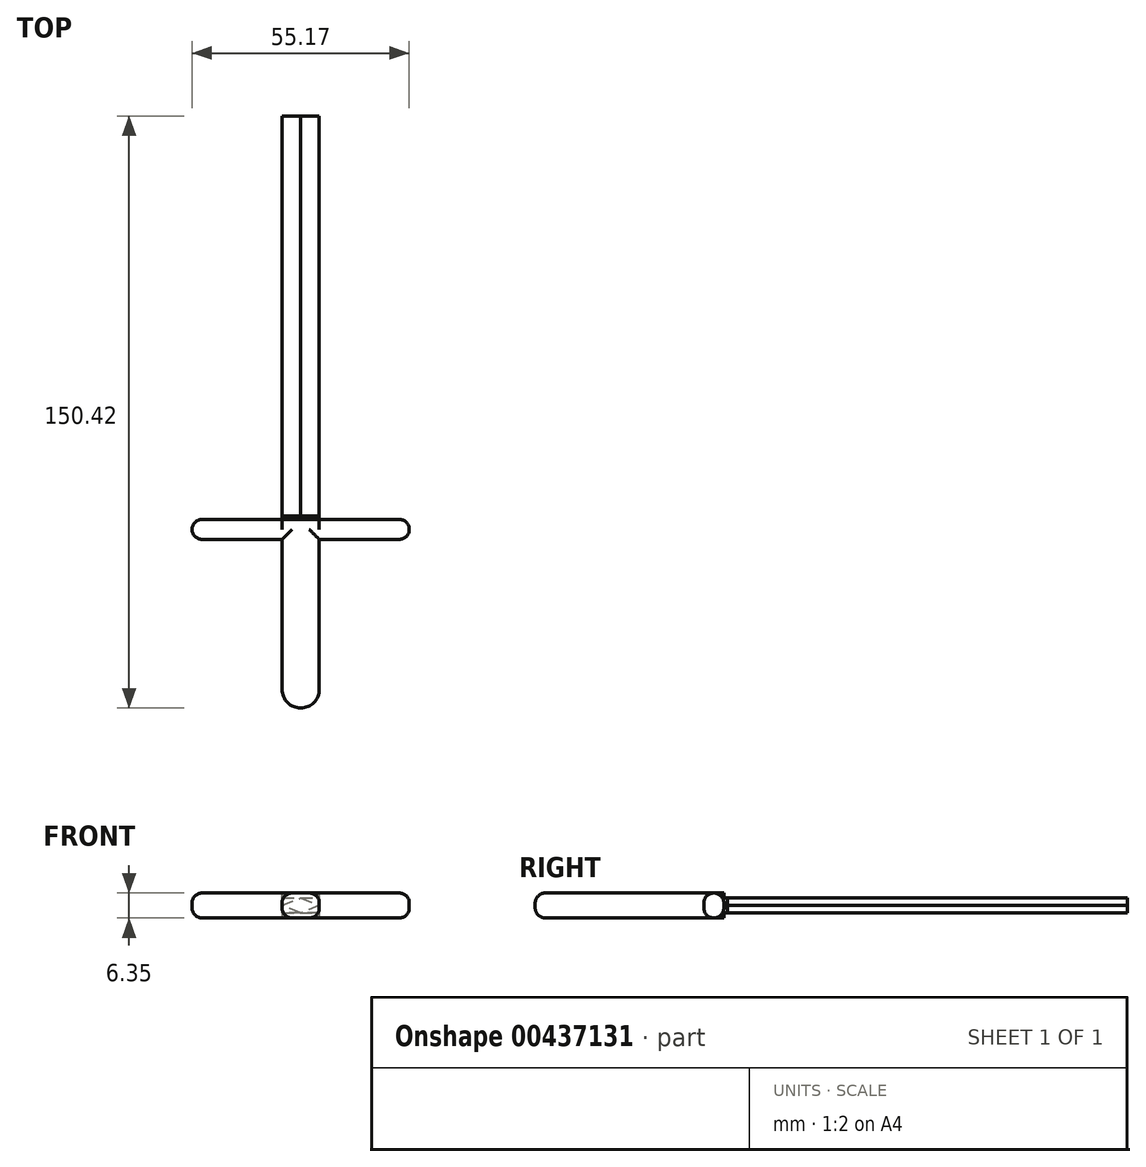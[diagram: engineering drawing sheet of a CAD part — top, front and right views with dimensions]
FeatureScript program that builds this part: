
annotation { "Feature Type Name" : "Feature", "Feature Type Description" : "" }
export const myFeature = defineFeature(function(context is Context, id is Id, definition is map)
    precondition{}
    {
        {
            var Q0;
            Q0=qCreatedBy(makeId("Top.planeOp"),FACE);
            var sketch = newSketch(context, id + "F0", { "sketchPlane" : qUnion([Q0])});
            skLineSegment(sketch, "E0.bottom", {"start": v(0, 0) * mm, "end": v(9.45, 0) * mm});
            skLineSegment(sketch, "E0.top", {"start": v(0, 62.33) * mm, "end": v(9.45, 62.33) * mm});
            skLineSegment(sketch, "E0.left", {"start": v(0, 0) * mm, "end": v(0, 62.33) * mm});
            skLineSegment(sketch, "E0.right", {"start": v(9.45, 0) * mm, "end": v(9.45, 62.33) * mm});
            skLineSegment(sketch, "E1", {"start": v(4.72, 0) * mm, "end": v(4.72, 75.05) * mm});
            skPoint(sketch, "E1.endSnap0", {"position": v(4.72, 62.33) * mm});
            skLineSegment(sketch, "E2", {"start": v(4.72, 75.05) * mm, "end": v(0, 62.33) * mm});
            skLineSegment(sketch, "E3", {"start": v(9.45, 62.33) * mm, "end": v(4.72, 75.05) * mm});
            skLineSegment(sketch, "E4", {"start": v(9.45, 0) * mm, "end": v(29.77, 0) * mm});
            skLineSegment(sketch, "E5", {"start": v(29.77, 0) * mm, "end": v(29.77, -5.08) * mm});
            skLineSegment(sketch, "E6", {"start": v(29.77, -5.08) * mm, "end": v(0, -5.08) * mm});
            skLineSegment(sketch, "E7", {"start": v(0, -5.08) * mm, "end": v(-20.32, -5.08) * mm});
            skLineSegment(sketch, "E8", {"start": v(-20.32, -5.08) * mm, "end": v(-20.32, 0) * mm});
            skLineSegment(sketch, "E9", {"start": v(-20.32, 0) * mm, "end": v(0, 0) * mm});
            skCircle(sketch, "E10", {"center": v(-20.32, -2.54) * mm, "radius": 2.54 * mm});
            skCircle(sketch, "E11", {"center": v(29.77, -2.54) * mm, "radius": 2.54 * mm});
            skLineSegment(sketch, "E12", {"start": v(0, -5.08) * mm, "end": v(0, -43.18) * mm});
            skLineSegment(sketch, "E13", {"start": v(0, -43.18) * mm, "end": v(9.45, -43.18) * mm});
            skLineSegment(sketch, "E14", {"start": v(9.45, -43.18) * mm, "end": v(9.45, -5.08) * mm});
            skCircle(sketch, "E15", {"center": v(4.72, -43.18) * mm, "radius": 4.72 * mm});
            skSolve(sketch);
        }
        {
            var Q0;
            {var subQ0=sQuery(id+"F0.wireOp",EDGE,"E0.left");Q0=makeQuery(id+"F0.imprint","IMPRINT",FACE,{"disambiguationData":[TD([[makeQuery(id+"F0.imprint","IMPRINT",EDGE,{"derivedFrom":subQ0}),-1.0]])]});}
            var Q1;
            {var subQ0=sQuery(id+"F0.wireOp",EDGE,"E0.right");Q1=makeQuery(id+"F0.imprint","IMPRINT",FACE,{"disambiguationData":[TD([[makeQuery(id+"F0.imprint","IMPRINT",EDGE,{"derivedFrom":subQ0}),1.0]])]});}
            var Q2;
            {var subQ0=sQuery(id+"F0.wireOp",EDGE,"E3");Q2=makeQuery(id+"F0.imprint","IMPRINT",FACE,{"disambiguationData":[TD([[makeQuery(id+"F0.imprint","IMPRINT",EDGE,{"derivedFrom":subQ0}),1.0]])]});}
            var Q3;
            {var subQ0=sQuery(id+"F0.wireOp",EDGE,"E2");Q3=makeQuery(id+"F0.imprint","IMPRINT",FACE,{"disambiguationData":[TD([[makeQuery(id+"F0.imprint","IMPRINT",EDGE,{"derivedFrom":subQ0}),1.0]])]});}
            var Q4;
            {var subQ5=sQuery(id+"F0.wireOp",EDGE,"E4");Q4=makeQuery(id+"F0.imprint","IMPRINT",FACE,{"disambiguationData":[TD([[makeQuery(id+"F0.imprint","IMPRINT",EDGE,{"derivedFrom":subQ5}),-1.0]])]});}
            var Q5;
            {var subQ0=sQuery(id+"F0.wireOp",EDGE,"E12");Q5=makeQuery(id+"F0.imprint","IMPRINT",FACE,{"disambiguationData":[TD([[makeQuery(id+"F0.imprint","IMPRINT",EDGE,{"derivedFrom":subQ0}),1.0]])]});}
            var Q6;
            {var subQ0=sQuery(id+"F0.wireOp",EDGE,"E8");Q6=makeQuery(id+"F0.imprint","IMPRINT",FACE,{"disambiguationData":[TD([[makeQuery(id+"F0.imprint","IMPRINT",EDGE,{"derivedFrom":subQ0}),-1.0]])]});}
            var Q7;
            {var subQ0=sQuery(id+"F0.wireOp",EDGE,"E8");Q7=makeQuery(id+"F0.imprint","IMPRINT",FACE,{"disambiguationData":[TD([[makeQuery(id+"F0.imprint","IMPRINT",EDGE,{"derivedFrom":subQ0}),1.0]])]});}
            var Q8;
            {var subQ0=sQuery(id+"F0.wireOp",EDGE,"E5");Q8=makeQuery(id+"F0.imprint","IMPRINT",FACE,{"disambiguationData":[TD([[makeQuery(id+"F0.imprint","IMPRINT",EDGE,{"derivedFrom":subQ0}),-1.0]])]});}
            var Q9;
            {var subQ0=sQuery(id+"F0.wireOp",EDGE,"E5");Q9=makeQuery(id+"F0.imprint","IMPRINT",FACE,{"disambiguationData":[TD([[makeQuery(id+"F0.imprint","IMPRINT",EDGE,{"derivedFrom":subQ0}),1.0]])]});}
            var Q10;
            {var subQ0=sQuery(id+"F0.wireOp",EDGE,"E13");Q10=makeQuery(id+"F0.imprint","IMPRINT",FACE,{"disambiguationData":[TD([[makeQuery(id+"F0.imprint","IMPRINT",EDGE,{"derivedFrom":subQ0}),-1.0]])]});}
            var Q11;
            {var subQ0=sQuery(id+"F0.wireOp",EDGE,"E13");Q11=makeQuery(id+"F0.imprint","IMPRINT",FACE,{"disambiguationData":[TD([[makeQuery(id+"F0.imprint","IMPRINT",EDGE,{"derivedFrom":subQ0}),1.0]])]});}
            extrude(context, id + "F1", {"entities" : qUnion([Q0, Q1, Q2, Q3, Q4, Q5, Q6, Q7, Q8, Q9, Q10, Q11]), "depth" : 6.35 * mm});
        }
        {
            var Q0;
            Q0=makeQuery(id+"F1.opExtrude","CAP_EDGE",EDGE,{"disambiguationData":[OSD([sQuery(id+"F0.wireOp",EDGE,"E12")])],"isStart":false});
            var Q1;
            Q1=makeQuery(id+"F1.opExtrude","CAP_EDGE",EDGE,{"disambiguationData":[OSD([sQuery(id+"F0.wireOp",EDGE,"E14")])],"isStart":false});
            var Q2;
            Q2=makeQuery(id+"F1.opExtrude","CAP_EDGE",EDGE,{"disambiguationData":[OSD([sQuery(id+"F0.wireOp",EDGE,"E12")])],"isStart":true});
            var Q3;
            Q3=makeQuery(id+"F1.opExtrude","CAP_EDGE",EDGE,{"disambiguationData":[OSD([sQuery(id+"F0.wireOp",EDGE,"E14")])],"isStart":true});
            var Q4;
            Q4=makeQuery(id+"F1.opExtrude","CAP_EDGE",EDGE,{"disambiguationData":[OSD([sQuery(id+"F0.wireOp",EDGE,"E6")])],"isStart":true});
            var Q5;
            Q5=makeQuery(id+"F1.opExtrude","CAP_EDGE",EDGE,{"disambiguationData":[OSD([sQuery(id+"F0.wireOp",EDGE,"E4")])],"isStart":true});
            var Q6;
            Q6=makeQuery(id+"F1.opExtrude","CAP_EDGE",EDGE,{"disambiguationData":[OSD([sQuery(id+"F0.wireOp",EDGE,"E9")])],"isStart":true});
            var Q7;
            Q7=makeQuery(id+"F1.opExtrude","CAP_EDGE",EDGE,{"disambiguationData":[OSD([sQuery(id+"F0.wireOp",EDGE,"E6")])],"isStart":false});
            var Q8;
            Q8=makeQuery(id+"F1.opExtrude","CAP_EDGE",EDGE,{"disambiguationData":[OSD([sQuery(id+"F0.wireOp",EDGE,"E4")])],"isStart":false});
            var Q9;
            Q9=makeQuery(id+"F1.opExtrude","CAP_EDGE",EDGE,{"disambiguationData":[OSD([sQuery(id+"F0.wireOp",EDGE,"E7")])],"isStart":false});
            var Q10;
            Q10=makeQuery(id+"F1.opExtrude","CAP_EDGE",EDGE,{"disambiguationData":[OSD([sQuery(id+"F0.wireOp",EDGE,"E9")])],"isStart":false});
            var Q11;
            Q11=makeQuery(id+"F1.opExtrude","CAP_EDGE",EDGE,{"disambiguationData":[OSD([sQuery(id+"F0.wireOp",EDGE,"E7")])],"isStart":true});
            fillet(context, id + "F2", {"entities" : qUnion([Q0, Q1, Q2, Q3, Q4, Q5, Q6, Q7, Q8, Q9, Q10, Q11]), "radius" : 2.54 * mm, "tangentPropagation" : true, "allowEdgeOverflow" : false});
        }
        {
            var Q0;
            Q0=makeQuery(id+"F1.opExtrude","CAP_FACE",FACE,{"disambiguationData":[OSD([sQuery(id+"F0.wireOp",EDGE,"E0.left"),sQuery(id+"F0.wireOp",EDGE,"E0.right"),sQuery(id+"F0.wireOp",EDGE,"E2"),sQuery(id+"F0.wireOp",EDGE,"E3"),sQuery(id+"F0.wireOp",EDGE,"E4"),sQuery(id+"F0.wireOp",EDGE,"E6"),sQuery(id+"F0.wireOp",EDGE,"E7"),sQuery(id+"F0.wireOp",EDGE,"E9"),sQuery(id+"F0.wireOp",EDGE,"E10"),sQuery(id+"F0.wireOp",EDGE,"E11"),sQuery(id+"F0.wireOp",EDGE,"E12"),sQuery(id+"F0.wireOp",EDGE,"E14"),sQuery(id+"F0.wireOp",EDGE,"E15")])],"isStart":false});
            var sketch = newSketch(context, id + "F3", { "sketchPlane" : qUnion([Q0])});
            skLineSegment(sketch, "E16", {"start": v(0, 0) * mm, "end": v(9.45, 0) * mm});
            skSolve(sketch);
        }
        {
            var Q0;
            {var subQ2=sQuery(id+"F3.wireOp",EDGE,"E16");Q0=makeQuery(id+"F3.imprint","IMPRINT",FACE,{"disambiguationData":[TD([[makeQuery(id+"F3.imprint","IMPRINT",EDGE,{"derivedFrom":subQ2}),1.0]])]});}
            extrude(context, id + "F4", {"entities" : qUnion([Q0]), "operationType" : NewBodyOperationType.REMOVE, "oppositeDirection" : true, "depth" : 1.27 * mm});
        }
        {
            var Q0;
            Q0=makeQuery(id+"F1.opExtrude","CAP_FACE",FACE,{"disambiguationData":[OSD([sQuery(id+"F0.wireOp",EDGE,"E0.left"),sQuery(id+"F0.wireOp",EDGE,"E0.right"),sQuery(id+"F0.wireOp",EDGE,"E2"),sQuery(id+"F0.wireOp",EDGE,"E3"),sQuery(id+"F0.wireOp",EDGE,"E4"),sQuery(id+"F0.wireOp",EDGE,"E6"),sQuery(id+"F0.wireOp",EDGE,"E7"),sQuery(id+"F0.wireOp",EDGE,"E9"),sQuery(id+"F0.wireOp",EDGE,"E10"),sQuery(id+"F0.wireOp",EDGE,"E11"),sQuery(id+"F0.wireOp",EDGE,"E12"),sQuery(id+"F0.wireOp",EDGE,"E14"),sQuery(id+"F0.wireOp",EDGE,"E15")])],"isStart":true});
            var sketch = newSketch(context, id + "F5", { "sketchPlane" : qUnion([Q0])});
            skLineSegment(sketch, "E17", {"start": v(0, 0) * mm, "end": v(9.45, 0) * mm});
            skSolve(sketch);
        }
        {
            var Q0;
            {var subQ2=sQuery(id+"F5.wireOp",EDGE,"E17");Q0=makeQuery(id+"F5.imprint","IMPRINT",FACE,{"disambiguationData":[TD([[makeQuery(id+"F5.imprint","IMPRINT",EDGE,{"derivedFrom":subQ2}),-1.0]])]});}
            extrude(context, id + "F6", {"entities" : qUnion([Q0]), "operationType" : NewBodyOperationType.REMOVE, "oppositeDirection" : true, "depth" : 1.27 * mm});
        }
        {
            var Q0;
            Q0=makeQuery(id+"F4.boolean.opBoolean","COPY",FACE,{"derivedFrom":makeQuery(id+"F4.opExtrude","CAP_FACE",FACE,{"disambiguationData":[OSD([sQuery(id+"F0.wireOp",EDGE,"E0.left"),sQuery(id+"F0.wireOp",EDGE,"E0.right"),sQuery(id+"F0.wireOp",EDGE,"E2"),sQuery(id+"F0.wireOp",EDGE,"E3"),sQuery(id+"F3.wireOp",EDGE,"E16")])],"isStart":false})});
            var sketch = newSketch(context, id + "F7", { "sketchPlane" : qUnion([Q0])});
            skLineSegment(sketch, "E18", {"start": v(0, 62.33) * mm, "end": v(9.45, 62.33) * mm});
            skSolve(sketch);
        }
        {
            var Q0;
            Q0=makeQuery(id+"F7.imprint","IMPRINT",FACE,{"disambiguationData":[TD([[makeQuery(id+"F7.imprint","IMPRINT",EDGE,{"derivedFrom":sQuery(id+"F7.wireOp",EDGE,"E18")}),1.0]])]});
            extrude(context, id + "F8", {"entities" : qUnion([Q0]), "operationType" : NewBodyOperationType.REMOVE, "oppositeDirection" : true, "depth" : 25.4 * mm});
        }
        {
            var Q0;
            Q0=makeQuery(id+"F8.boolean.opBoolean","COPY",FACE,{"derivedFrom":makeQuery(id+"F8.opExtrude","SWEPT_FACE",FACE,{"disambiguationData":[OSD([sQuery(id+"F7.wireOp",EDGE,"E18")])]})});
            extrude(context, id + "F9", {"entities" : qUnion([Q0]), "operationType" : NewBodyOperationType.ADD, "depth" : 50.8 * mm});
        }
        {
            var Q0;
            Q0=makeQuery(id+"F9.boolean.opBoolean","MERGE",FACE,{"derivedFrom":[makeQuery(id+"F4.boolean.opBoolean","COPY",FACE,{"derivedFrom":makeQuery(id+"F4.opExtrude","CAP_FACE",FACE,{"disambiguationData":[OSD([sQuery(id+"F0.wireOp",EDGE,"E0.left"),sQuery(id+"F0.wireOp",EDGE,"E0.right"),sQuery(id+"F0.wireOp",EDGE,"E2"),sQuery(id+"F0.wireOp",EDGE,"E3"),sQuery(id+"F3.wireOp",EDGE,"E16")])],"isStart":false})}),makeQuery(id+"F9.opExtrude","SWEPT_FACE",FACE,{"disambiguationData":[OSD([sQuery(id+"F7.wireOp",EDGE,"E18")])]})]});
            var sketch = newSketch(context, id + "F10", { "sketchPlane" : qUnion([Q0])});
            skLineSegment(sketch, "E19", {"start": v(4.72, 113.13) * mm, "end": v(0, 102.52) * mm});
            skLineSegment(sketch, "E20", {"start": v(0, 102.52) * mm, "end": v(9.45, 102.52) * mm});
            skLineSegment(sketch, "E21", {"start": v(9.45, 102.52) * mm, "end": v(4.72, 113.13) * mm});
            skSolve(sketch);
        }
        {
            var Q0;
            {var subQ0=sQuery(id+"F10.wireOp",EDGE,"E19");Q0=makeQuery(id+"F10.imprint","IMPRINT",FACE,{"disambiguationData":[TD([[makeQuery(id+"F10.imprint","IMPRINT",EDGE,{"derivedFrom":subQ0}),-1.0]])]});}
            var Q1;
            {var subQ0=sQuery(id+"F10.wireOp",EDGE,"E21");Q1=makeQuery(id+"F10.imprint","IMPRINT",FACE,{"disambiguationData":[TD([[makeQuery(id+"F10.imprint","IMPRINT",EDGE,{"derivedFrom":subQ0}),-1.0]])]});}
            extrude(context, id + "F11", {"entities" : qUnion([Q0, Q1]), "operationType" : NewBodyOperationType.REMOVE, "oppositeDirection" : true, "depth" : 25.4 * mm});
        }
        {
            var Q0;
            Q0=makeQuery(id+"F9.boolean.opBoolean","MERGE",FACE,{"derivedFrom":[makeQuery(id+"F4.boolean.opBoolean","COPY",FACE,{"derivedFrom":makeQuery(id+"F4.opExtrude","CAP_FACE",FACE,{"disambiguationData":[OSD([sQuery(id+"F0.wireOp",EDGE,"E0.left"),sQuery(id+"F0.wireOp",EDGE,"E0.right"),sQuery(id+"F0.wireOp",EDGE,"E2"),sQuery(id+"F0.wireOp",EDGE,"E3"),sQuery(id+"F3.wireOp",EDGE,"E16")])],"isStart":false})}),makeQuery(id+"F9.opExtrude","SWEPT_FACE",FACE,{"disambiguationData":[OSD([sQuery(id+"F7.wireOp",EDGE,"E18")])]})]});
            var sketch = newSketch(context, id + "F12", { "sketchPlane" : qUnion([Q0])});
            skLineSegment(sketch, "E22", {"start": v(0, 102.52) * mm, "end": v(9.45, 102.52) * mm});
            skSolve(sketch);
        }
        {
            var Q0;
            Q0=makeQuery(id+"F12.imprint","IMPRINT",FACE,{"disambiguationData":[TD([[makeQuery(id+"F12.imprint","IMPRINT",EDGE,{"derivedFrom":sQuery(id+"F12.wireOp",EDGE,"E22")}),1.0]])]});
            extrude(context, id + "F13", {"entities" : qUnion([Q0]), "operationType" : NewBodyOperationType.REMOVE, "oppositeDirection" : true, "depth" : 25.4 * mm});
        }
        {
            var Q0;
            Q0=makeQuery(id+"F13.boolean.opBoolean","COPY",FACE,{"derivedFrom":makeQuery(id+"F13.opExtrude","SWEPT_FACE",FACE,{"disambiguationData":[OSD([sQuery(id+"F12.wireOp",EDGE,"E22")])]})});
            var sketch = newSketch(context, id + "F14", { "sketchPlane" : qUnion([Q0])});
            skLineSegment(sketch, "E23", {"start": v(-4.72, 5.08) * mm, "end": v(-9.45, 3.17) * mm});
            skLineSegment(sketch, "E24", {"start": v(-9.45, 3.17) * mm, "end": v(-4.72, 1.27) * mm});
            skLineSegment(sketch, "E25", {"start": v(-4.72, 1.27) * mm, "end": v(0, 3.17) * mm});
            skLineSegment(sketch, "E26", {"start": v(0, 3.17) * mm, "end": v(-4.72, 5.08) * mm});
            skSolve(sketch);
        }
        {
            var Q0;
            {var subQ0=sQuery(id+"F14.wireOp",EDGE,"E26");Q0=makeQuery(id+"F14.imprint","IMPRINT",FACE,{"disambiguationData":[TD([[makeQuery(id+"F14.imprint","IMPRINT",EDGE,{"derivedFrom":subQ0}),-1.0]])]});}
            var Q1;
            {var subQ0=sQuery(id+"F14.wireOp",EDGE,"E25");Q1=makeQuery(id+"F14.imprint","IMPRINT",FACE,{"disambiguationData":[TD([[makeQuery(id+"F14.imprint","IMPRINT",EDGE,{"derivedFrom":subQ0}),-1.0]])]});}
            var Q2;
            {var subQ0=sQuery(id+"F14.wireOp",EDGE,"E24");Q2=makeQuery(id+"F14.imprint","IMPRINT",FACE,{"disambiguationData":[TD([[makeQuery(id+"F14.imprint","IMPRINT",EDGE,{"derivedFrom":subQ0}),-1.0]])]});}
            var Q3;
            {var subQ0=sQuery(id+"F14.wireOp",EDGE,"E23");Q3=makeQuery(id+"F14.imprint","IMPRINT",FACE,{"disambiguationData":[TD([[makeQuery(id+"F14.imprint","IMPRINT",EDGE,{"derivedFrom":subQ0}),-1.0]])]});}
            extrude(context, id + "F15", {"entities" : qUnion([Q0, Q1, Q2, Q3]), "operationType" : NewBodyOperationType.REMOVE, "oppositeDirection" : true, "depth" : 101.6 * mm});
        }
    });
